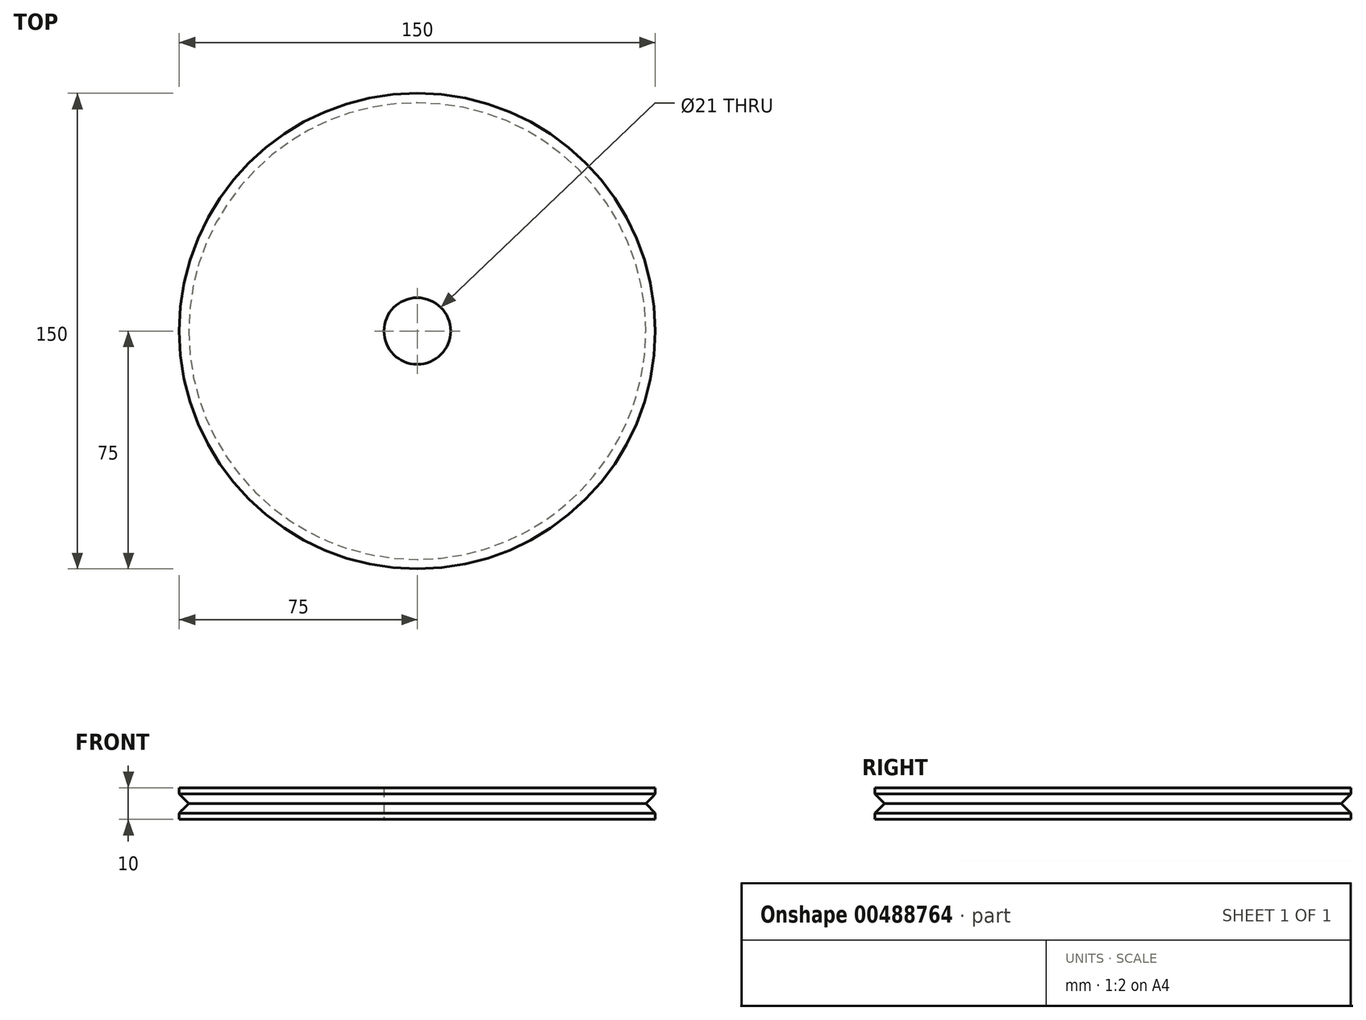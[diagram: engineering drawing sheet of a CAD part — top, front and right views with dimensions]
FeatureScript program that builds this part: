
annotation { "Feature Type Name" : "Feature", "Feature Type Description" : "" }
export const myFeature = defineFeature(function(context is Context, id is Id, definition is map)
    precondition{}
    {
        {
            var Q0;
            Q0=qCreatedBy(makeId("Top.planeOp"),FACE);
            var sketch = newSketch(context, id + "F0", { "sketchPlane" : qUnion([Q0])});
            skCircle(sketch, "E0", {"center": v(0, 0) * mm, "radius": 75 * mm});
            skSolve(sketch);
        }
        {
            var Q0;
            Q0 = qSketchRegion(id + "F0", true);
            extrude(context, id + "F1", {"entities" : qUnion([Q0]), "depth" : 5 * mm});
        }
        {
            var Q0;
            Q0=makeQuery(id+"F1.opExtrude","CAP_EDGE",EDGE,{"disambiguationData":[OSD([sQuery(id+"F0.wireOp",EDGE,"E0")])],"isStart":true});
            chamfer(context, id + "F2", {"entities" : qUnion([Q0]), "width" : 3 * mm, "tangentPropagation" : true});
        }
        {
            var Q0;
            Q0=makeQuery(id+"F1.opExtrude","CAP_FACE",FACE,{"disambiguationData":[OSD([sQuery(id+"F0.wireOp",EDGE,"E0")])],"isStart":true});
            var sketch = newSketch(context, id + "F3", { "sketchPlane" : qUnion([Q0])});
            skCircle(sketch, "E1", {"center": v(0, 0) * mm, "radius": 75 * mm});
            skSolve(sketch);
        }
        {
            var Q0;
            Q0 = qSketchRegion(id + "F3", true);
            extrude(context, id + "F4", {"entities" : qUnion([Q0]), "operationType" : NewBodyOperationType.ADD, "depth" : 5 * mm});
        }
        {
            var Q0;
            Q0=makeQuery(id+"F4.opExtrude","CAP_EDGE",EDGE,{"disambiguationData":[OSD([sQuery(id+"F3.wireOp",EDGE,"E1")])],"isStart":true});
            chamfer(context, id + "F5", {"entities" : qUnion([Q0]), "width" : 3 * mm, "tangentPropagation" : true});
        }
        {
            var Q0;
            Q0=makeQuery(id+"F4.opExtrude","CAP_FACE",FACE,{"disambiguationData":[OSD([sQuery(id+"F3.wireOp",EDGE,"E1")])],"isStart":false});
            var sketch = newSketch(context, id + "F6", { "sketchPlane" : qUnion([Q0])});
            skCircle(sketch, "E2", {"center": v(0, 0) * mm, "radius": 10.5 * mm});
            skSolve(sketch);
        }
        {
            var Q0;
            Q0=makeQuery(id+"F6.imprint","IMPRINT",FACE,{"disambiguationData":[TD([[makeQuery(id+"F6.imprint","IMPRINT",EDGE,{"derivedFrom":sQuery(id+"F6.wireOp",EDGE,"E2")}),1.0]])]});
            extrude(context, id + "F7", {"entities" : qUnion([Q0]), "operationType" : NewBodyOperationType.REMOVE, "oppositeDirection" : true, "depth" : 127 * mm});
        }
    });
